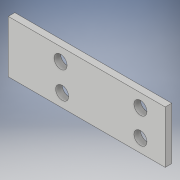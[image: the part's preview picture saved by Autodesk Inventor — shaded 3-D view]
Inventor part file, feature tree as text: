
AUTODESK INVENTOR PART (.ipt)
format: ipt  version: 2017 (Build 210142000, 142)  size: 105,472 bytes
history: native  units: in
note: dims shown in document units (in); Inventor stores cm internally (conversion verified against a paired STEP export)
features: extrude x1, sketch x1
ambient origin geometry x8: Origin, YZ Plane, XZ Plane, XY Plane, X Axis, Y Axis, Z Axis, Center Point
bodies: Solid1 (feature_tree)
feature tree (2):
  extrude  "Extrusion1"  Depth=1.0in
  sketch  "Sketch1"  dims[d0=3.0in d1=1.0in d2=0.25in d3=0.25in d4=0.5in d5=0.25in d6=1.0in d7=0.25in d8=0.25in d9=0.5in d10=0.125in d11=0.0in]
